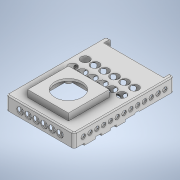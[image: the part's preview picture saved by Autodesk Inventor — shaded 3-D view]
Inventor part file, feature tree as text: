
AUTODESK INVENTOR PART (.ipt)
format: ipt  version: 2020 (Build 240168000, 168)  size: 851,968 bytes
history: native  units: mm
features: extrude x18, sketch x14, revolve x9, mirror x2, fillet x1, plane x1
ambient origin geometry x8: Origin, YZ Plane, XZ Plane, XY Plane, X Axis, Y Axis, Z Axis, Center Point
bodies: Solid1 (feature_tree)
feature tree (45):
  sketch  "Sketch1"  dims[d2=60.0mm d3=88.0mm]
  extrude  "Extrusion1"  Depth=88.0mm
  extrude  "Extrusion2"  Depth=56.0mm
  extrude  "Extrusion3"  Depth=3.0mm
  sketch  "Sketch3"  dims[d6=3.0mm d7=2.0mm]
  extrude  "Extrusion4"  Depth=8.0mm TaperAngle=0.0deg
  extrude  "Extrusion5"  Depth=4.0mm
  extrude  "Extrusion6"  Depth=19.0mm TaperAngle=0.0deg
  sketch  "Sketch5"  dims[d12=4.0mm d13=4.0mm]
  extrude  "Extrusion7"  Depth=2.5mm
  fillet  "Fillet1"  Radius=21.0mm
  sketch  "Sketch8"  dims[d17=16.0mm d18=2.5mm d19=21.0mm d20=0.0mm]
  extrude  "Extrusion8"  Depth=5.0mm
  extrude  "Extrusion9"  Depth=7.0mm
  extrude  "Extrusion10"  Depth=10.0mm
  extrude  "Extrusion11"  Depth=8.0mm
  extrude  "Extrusion12"  Depth=8.0mm
  sketch  "Sketch10"  dims[d28=32.5mm d29=7.0mm]
  extrude  "Extrusion13"  Depth=10.0mm
  extrude  "Extrusion14"  Depth=3.0mm TaperAngle=0.0deg
  extrude  "Extrusion15"  Depth=3.0mm
  plane  "Work Plane1"
  mirror  "Mirror1"
  sketch  "Sketch11"  dims[d30=10.0mm d31=0.0mm d32=1.7mm]
  extrude  "Extrusion16"  Depth=3.0mm
  extrude  "Extrusion17"  Depth=3.0mm
  extrude  "Extrusion18"  TaperAngle=45.0deg  [1 undecoded]
  sketch  "Sketch14"  dims[d33=10.5mm d34=8.0mm]
  revolve  "Revolution18"  [1 undecoded]
  revolve  "Revolution19"  [1 undecoded]
  revolve  "Revolution20"  [1 undecoded]
  revolve  "Revolution21"  [1 undecoded]
  revolve  "Revolution22"  [1 undecoded]
  revolve  "Revolution23"  [1 undecoded]
  sketch  "Sketch17"  dims[d35=5.0mm d36=8.0mm]
  sketch  "Sketch18"  dims[d37=5.0mm d38=10.0mm]
  sketch  "Sketch19"  dims[d39=1.7mm d40=2.0mm d41=0.0mm d42=1.0mm d43=25.0mm d44=17.0mm d45=45.0deg d46=2.5mm d47=2.5mm d48=34.0mm d49=34.0mm d50=36.0mm d51=36.0mm d52=10.0mm d53=0.0mm d54=8.0mm d55=0.0mm d56=5.0mm d57=5.0mm d58=5.0mm d59=5.0mm d60=8.0mm d61=0.0mm d62=4.0mm d63=0.0mm d64=24.0mm d65=4.0mm d66=0.0mm d67=6.0mm d68=6.0mm d69=6.0mm d70=6.0mm d71=6.0mm d72=6.0mm d73=6.0mm d74=6.0mm d75=6.0mm d76=6.0mm d77=6.0mm d78=6.0mm d79=6.0mm d80=4.0mm d81=3.0mm d82=3.0mm d83=3.0mm d84=3.0mm d85=3.0mm d86=3.0mm d87=3.0mm d88=3.0mm d89=3.0mm d90=3.0mm d91=3.0mm d92=3.0mm d93=3.0mm d94=3.0mm d95=3.0mm d96=0.0mm d97=1.0mm d98=0.0mm d99=1.0mm d100=0.0mm d101=7.0mm d102=7.0mm d103=7.0mm d104=7.0mm d105=7.0mm d106=7.0mm d107=7.0mm d108=6.0mm d109=3.5mm d110=3.5mm d111=3.5mm d112=3.5mm d113=3.5mm d114=3.5mm d115=1.5mm d116=0.0mm d117=0.75mm d118=0.0mm d119=0.75mm d120=0.0mm d134=6.0mm d140=6.0mm d144=6.0mm d148=6.0mm d152=25.0mm d153=18.0mm d154=7.5mm d155=4.5mm d156=7.5mm d158=60.0deg d159=60.0deg d196=90.0deg d197=90.0deg d198=90.0deg d199=90.0deg d200=90.0deg d201=90.0deg d202=90.0deg d203=90.0deg d204=90.0deg d205=0.0mm]
  revolve  "Revolution24"  [1 undecoded]
  revolve  "Revolution25"  [1 undecoded]
  revolve  "Revolution26"  [1 undecoded]
  mirror  "Mirror4"
  sketch  "Sketch2"  dims[d4=56.0mm d5=85.0mm]
  sketch  "Sketch4"  dims[d8=4.0mm d9=0.0mm d10=8.0mm d11=0.0mm]
  sketch  "Sketch6"  dims[d14=11.0mm d15=19.0mm d16=0.0mm]
  sketch  "Sketch9"  dims[d21=5.0mm d22=0.0mm d27=2.5mm]
note: 10 required parameter values undecoded (feature->parameter linkage not recoverable at this tier; creation-order binding heuristic only, values carry confidence <= 0.55)